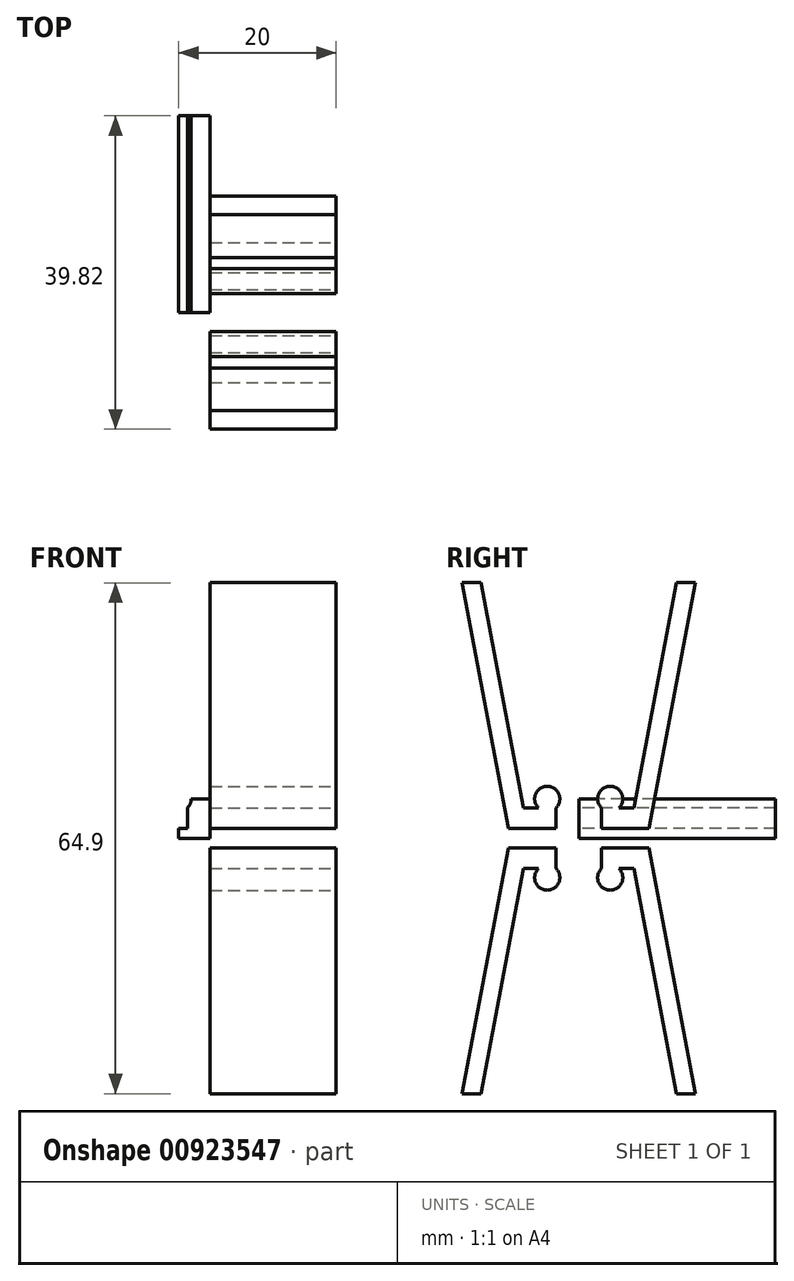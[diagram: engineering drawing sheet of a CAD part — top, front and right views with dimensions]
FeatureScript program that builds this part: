
annotation { "Feature Type Name" : "Feature", "Feature Type Description" : "" }
export const myFeature = defineFeature(function(context is Context, id is Id, definition is map)
    precondition{}
    {
        {
            var Q0;
            Q0=qCreatedBy(makeId("Front.planeOp"),FACE);
            var sketch = newSketch(context, id + "F0", { "sketchPlane" : qUnion([Q0])});
            skLineSegment(sketch, "E0", {"start": v(-1.1, -1.16) * mm, "end": v(0, -1.16) * mm});
            skLineSegment(sketch, "E1", {"start": v(0, -1.16) * mm, "end": v(1.1, -1.16) * mm});
            skCircle(sketch, "E2", {"center": v(0, 0) * mm, "radius": 1.6 * mm});
            skPoint(sketch, "E2.third.point", {"position": v(0.04, 1.6) * mm});
            skLineSegment(sketch, "E3.bottom", {"start": v(1.1, -1.16) * mm, "end": v(-4.9, -1.16) * mm});
            skLineSegment(sketch, "E3.top", {"start": v(1.1, -3.76) * mm, "end": v(-4.9, -3.76) * mm});
            skLineSegment(sketch, "E3.left", {"start": v(1.1, -1.16) * mm, "end": v(1.1, -3.76) * mm});
            skLineSegment(sketch, "E3.right", {"start": v(-4.9, -1.16) * mm, "end": v(-4.9, -3.76) * mm});
            skLineSegment(sketch, "E4", {"start": v(-4.9, -3.76) * mm, "end": v(-10.82, 27.45) * mm});
            skLineSegment(sketch, "E5", {"start": v(-10.82, 27.45) * mm, "end": v(-8.44, 27.45) * mm});
            skLineSegment(sketch, "E6", {"start": v(-8.44, 27.45) * mm, "end": v(-3.01, -1.16) * mm});
            skSolve(sketch);
        }
        {
            var Q0;
            {var subQ0=sQuery(id+"F0.wireOp",EDGE,"E3.bottom");var subQ1=sQuery(id+"F0.wireOp",EDGE,"E2");var subQ3=makeQuery(id+"F0.imprint","INTERSECT",VERTEX,{"derivedFrom":[subQ1,subQ0]});Q0=makeQuery(id+"F0.imprint","IMPRINT",FACE,{"disambiguationData":[TD([[makeQuery(id+"F0.imprint","IMPRINT",EDGE,{"disambiguationData":[TD([[subQ3,1.0]])],"derivedFrom":subQ1}),1.0]])]});}
            var Q1;
            Q1=makeQuery(id+"F0.imprint","IMPRINT",FACE,{"disambiguationData":[TD([[makeQuery(id+"F0.imprint","IMPRINT",EDGE,{"derivedFrom":sQuery(id+"F0.wireOp",EDGE,"E3.top")}),-1.0]])]});
            var Q2;
            {var subQ0=sQuery(id+"F0.wireOp",EDGE,"E3.bottom");var subQ1=sQuery(id+"F0.wireOp",EDGE,"E2");var subQ3=makeQuery(id+"F0.imprint","INTERSECT",VERTEX,{"derivedFrom":[subQ1,subQ0]});Q2=makeQuery(id+"F0.imprint","IMPRINT",FACE,{"disambiguationData":[TD([[makeQuery(id+"F0.imprint","IMPRINT",EDGE,{"disambiguationData":[TD([[subQ3,-1.0]])],"derivedFrom":subQ1}),1.0]])]});}
            var Q3;
            {var subQ0=sQuery(id+"F0.wireOp",EDGE,"E3.right");Q3=makeQuery(id+"F0.imprint","IMPRINT",FACE,{"disambiguationData":[TD([[makeQuery(id+"F0.imprint","IMPRINT",EDGE,{"derivedFrom":subQ0}),-1.0]])]});}
            extrude(context, id + "F1", {"entities" : qUnion([Q0, Q1, Q2, Q3]), "depth" : 16 * mm, "offsetDistance" : 25 * mm});
        }
        {
            var Q0;
            Q0=makeQuery(id+"F1.opExtrude","CAP_FACE",FACE,{"disambiguationData":[OSD([sQuery(id+"F0.wireOp",EDGE,"E2"),sQuery(id+"F0.wireOp",EDGE,"E3.bottom"),sQuery(id+"F0.wireOp",EDGE,"E3.top"),sQuery(id+"F0.wireOp",EDGE,"E3.left"),sQuery(id+"F0.wireOp",EDGE,"O02EmMhx-rZte-Ui8f-6fCR-LSKg8qAi1tnY"),sQuery(id+"F0.wireOp",EDGE,"amxZPU7I-p2Pu-trbv-WmTD-SQuBfFTmDBNC"),sQuery(id+"F0.wireOp",EDGE,"Ek9QiuSt-BqBX-cIDf-lFYa-oonIefYqzXJ9")])],"isStart":false});
            var sketch = newSketch(context, id + "F2", { "sketchPlane" : qUnion([Q0])});
            skLineSegment(sketch, "E7.bottom", {"start": v(0, 0) * mm, "end": v(4, 0) * mm});
            skLineSegment(sketch, "E7.top", {"start": v(0, -5) * mm, "end": v(4, -5) * mm});
            skLineSegment(sketch, "E7.left", {"start": v(0, 0) * mm, "end": v(0, -5) * mm});
            skLineSegment(sketch, "E7.right", {"start": v(4, 0) * mm, "end": v(4, -5) * mm});
            skSolve(sketch);
        }
        {
            var Q0;
            {var subQ2=sQuery(id+"F2.wireOp",EDGE,"E7.top");Q0=makeQuery(id+"F2.imprint","IMPRINT",FACE,{"disambiguationData":[TD([[makeQuery(id+"F2.imprint","IMPRINT",EDGE,{"derivedFrom":subQ2}),1.0]])]});}
            extrude(context, id + "F3", {"entities" : qUnion([Q0]), "oppositeDirection" : true, "depth" : 25 * mm, "offsetDistance" : 25 * mm});
        }
        {
            var Q0;
            Q0=makeQuery(id+"F1.opExtrude","SWEPT_BODY",BODY,{"disambiguationData":[OSD([sQuery(id+"F0.wireOp",EDGE,"E2"),sQuery(id+"F0.wireOp",EDGE,"E3.bottom"),sQuery(id+"F0.wireOp",EDGE,"E3.top"),sQuery(id+"F0.wireOp",EDGE,"E3.left"),sQuery(id+"F0.wireOp",EDGE,"O02EmMhx-rZte-Ui8f-6fCR-LSKg8qAi1tnY"),sQuery(id+"F0.wireOp",EDGE,"amxZPU7I-p2Pu-trbv-WmTD-SQuBfFTmDBNC"),sQuery(id+"F0.wireOp",EDGE,"Ek9QiuSt-BqBX-cIDf-lFYa-oonIefYqzXJ9")])]});
            var Q1;
            Q1=makeQuery(id+"F3.opExtrude","SWEPT_FACE",FACE,{"disambiguationData":[OSD([sQuery(id+"F2.wireOp",EDGE,"E7.right")])]});
            mirror(context, id + "F4", {"entities" : qUnion([Q0]), "mirrorPlane" : qUnion([Q1])});
        }
        {
            var Q0;
            Q0=makeQuery(id+"F1.opExtrude","SWEPT_BODY",BODY,{"disambiguationData":[OSD([sQuery(id+"F0.wireOp",EDGE,"E2"),sQuery(id+"F0.wireOp",EDGE,"E3.bottom"),sQuery(id+"F0.wireOp",EDGE,"E3.top"),sQuery(id+"F0.wireOp",EDGE,"E3.left"),sQuery(id+"F0.wireOp",EDGE,"O02EmMhx-rZte-Ui8f-6fCR-LSKg8qAi1tnY"),sQuery(id+"F0.wireOp",EDGE,"amxZPU7I-p2Pu-trbv-WmTD-SQuBfFTmDBNC"),sQuery(id+"F0.wireOp",EDGE,"Ek9QiuSt-BqBX-cIDf-lFYa-oonIefYqzXJ9")])]});
            var Q1;
            Q1=makeQuery(id+"F4.opPattern","COPY",BODY,{"derivedFrom":makeQuery(id+"F1.opExtrude","SWEPT_BODY",BODY,{"disambiguationData":[OSD([sQuery(id+"F0.wireOp",EDGE,"E2"),sQuery(id+"F0.wireOp",EDGE,"E3.bottom"),sQuery(id+"F0.wireOp",EDGE,"E3.top"),sQuery(id+"F0.wireOp",EDGE,"E3.left"),sQuery(id+"F0.wireOp",EDGE,"O02EmMhx-rZte-Ui8f-6fCR-LSKg8qAi1tnY"),sQuery(id+"F0.wireOp",EDGE,"amxZPU7I-p2Pu-trbv-WmTD-SQuBfFTmDBNC"),sQuery(id+"F0.wireOp",EDGE,"Ek9QiuSt-BqBX-cIDf-lFYa-oonIefYqzXJ9")])]}),"instanceName":"1"});
            var Q2;
            Q2=makeQuery(id+"F3.opExtrude","SWEPT_FACE",FACE,{"disambiguationData":[OSD([sQuery(id+"F2.wireOp",EDGE,"E7.top")])]});
            mirror(context, id + "F5", {"entities" : qUnion([Q0, Q1]), "mirrorPlane" : qUnion([Q2])});
        }
        {
            var Q0;
            Q0=makeQuery(id+"F5.opPattern","COPY",BODY,{"derivedFrom":makeQuery(id+"F1.opExtrude","SWEPT_BODY",BODY,{"disambiguationData":[OSD([sQuery(id+"F0.wireOp",EDGE,"E2"),sQuery(id+"F0.wireOp",EDGE,"E3.bottom"),sQuery(id+"F0.wireOp",EDGE,"E3.top"),sQuery(id+"F0.wireOp",EDGE,"E3.left"),sQuery(id+"F0.wireOp",EDGE,"O02EmMhx-rZte-Ui8f-6fCR-LSKg8qAi1tnY"),sQuery(id+"F0.wireOp",EDGE,"amxZPU7I-p2Pu-trbv-WmTD-SQuBfFTmDBNC"),sQuery(id+"F0.wireOp",EDGE,"Ek9QiuSt-BqBX-cIDf-lFYa-oonIefYqzXJ9")])]}),"instanceName":"1"});
            var Q1;
            Q1=makeQuery(id+"F4.opPattern","COPY",BODY,{"derivedFrom":makeQuery(id+"F1.opExtrude","SWEPT_BODY",BODY,{"disambiguationData":[OSD([sQuery(id+"F0.wireOp",EDGE,"E2"),sQuery(id+"F0.wireOp",EDGE,"E3.bottom"),sQuery(id+"F0.wireOp",EDGE,"E3.top"),sQuery(id+"F0.wireOp",EDGE,"E3.left"),sQuery(id+"F0.wireOp",EDGE,"O02EmMhx-rZte-Ui8f-6fCR-LSKg8qAi1tnY"),sQuery(id+"F0.wireOp",EDGE,"amxZPU7I-p2Pu-trbv-WmTD-SQuBfFTmDBNC"),sQuery(id+"F0.wireOp",EDGE,"Ek9QiuSt-BqBX-cIDf-lFYa-oonIefYqzXJ9")])]}),"instanceName":"1"});
            var Q2;
            Q2=makeQuery(id+"F5.opPattern","COPY",BODY,{"derivedFrom":makeQuery(id+"F4.opPattern","COPY",BODY,{"derivedFrom":makeQuery(id+"F1.opExtrude","SWEPT_BODY",BODY,{"disambiguationData":[OSD([sQuery(id+"F0.wireOp",EDGE,"E2"),sQuery(id+"F0.wireOp",EDGE,"E3.bottom"),sQuery(id+"F0.wireOp",EDGE,"E3.top"),sQuery(id+"F0.wireOp",EDGE,"E3.left"),sQuery(id+"F0.wireOp",EDGE,"O02EmMhx-rZte-Ui8f-6fCR-LSKg8qAi1tnY"),sQuery(id+"F0.wireOp",EDGE,"amxZPU7I-p2Pu-trbv-WmTD-SQuBfFTmDBNC"),sQuery(id+"F0.wireOp",EDGE,"Ek9QiuSt-BqBX-cIDf-lFYa-oonIefYqzXJ9")])]}),"instanceName":"1"}),"instanceName":"1"});
            var Q3;
            Q3=makeQuery(id+"F1.opExtrude","SWEPT_BODY",BODY,{"disambiguationData":[OSD([sQuery(id+"F0.wireOp",EDGE,"E2"),sQuery(id+"F0.wireOp",EDGE,"E3.bottom"),sQuery(id+"F0.wireOp",EDGE,"E3.top"),sQuery(id+"F0.wireOp",EDGE,"E3.left"),sQuery(id+"F0.wireOp",EDGE,"O02EmMhx-rZte-Ui8f-6fCR-LSKg8qAi1tnY"),sQuery(id+"F0.wireOp",EDGE,"amxZPU7I-p2Pu-trbv-WmTD-SQuBfFTmDBNC"),sQuery(id+"F0.wireOp",EDGE,"Ek9QiuSt-BqBX-cIDf-lFYa-oonIefYqzXJ9")])]});
            var Q4;
            Q4=makeQuery(id+"F3.opExtrude","CAP_EDGE",EDGE,{"disambiguationData":[OSD([sQuery(id+"F2.wireOp",EDGE,"E7.right")])],"isStart":true});
            transform(context, id + "F6", {"entities" : qUnion([Q0, Q1, Q2, Q3]), "transformType" : TransformType.ROTATION, "transformAxis" : qUnion([Q4]), "angle" : 90 * degree, "makeCopy" : false});
        }
    });
